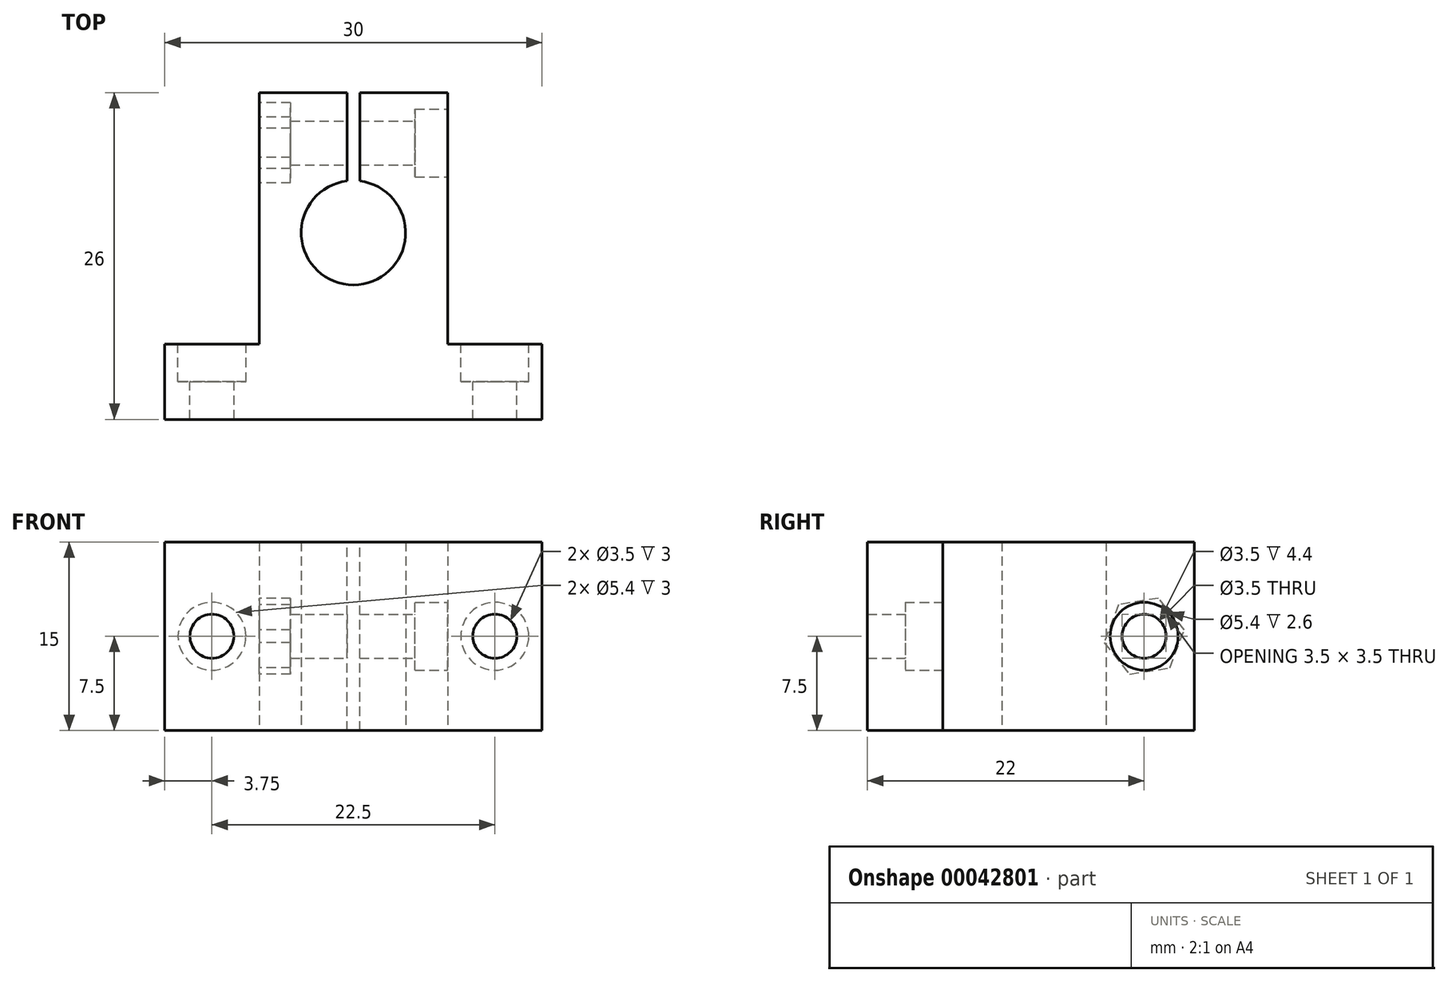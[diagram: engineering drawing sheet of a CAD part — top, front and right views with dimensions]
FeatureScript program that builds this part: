
annotation { "Feature Type Name" : "Feature", "Feature Type Description" : "" }
export const myFeature = defineFeature(function(context is Context, id is Id, definition is map)
    precondition{}
    {
        {
            var Q0;
            Q0=qCreatedBy(makeId("Top.planeOp"),FACE);
            var sketch = newSketch(context, id + "F0", { "sketchPlane" : qUnion([Q0])});
            skLineSegment(sketch, "E0.rect.bottom", {"start": v(-7.5, 10) * mm, "end": v(7.5, 10) * mm});
            skLineSegment(sketch, "E0.rect.left", {"start": v(-7.5, 10) * mm, "end": v(-7.5, -10) * mm});
            skLineSegment(sketch, "E0.rect.right", {"start": v(7.5, 10) * mm, "end": v(7.5, -10) * mm});
            skLineSegment(sketch, "E1.top", {"start": v(-15, -16) * mm, "end": v(15, -16) * mm});
            skLineSegment(sketch, "E1.left", {"start": v(-15, -10) * mm, "end": v(-15, -16) * mm});
            skLineSegment(sketch, "E1.right", {"start": v(15, -10) * mm, "end": v(15, -16) * mm});
            skLineSegment(sketch, "E2", {"start": v(-15, -10) * mm, "end": v(-7.5, -10) * mm});
            skLineSegment(sketch, "E3", {"start": v(7.5, -10) * mm, "end": v(15, -10) * mm});
            skCircle(sketch, "E4", {"center": v(0, -1.15) * mm, "radius": 4.15 * mm});
            skSolve(sketch);
        }
        {
            var Q0;
            {var subQ2=sQuery(id+"F0.wireOp",EDGE,"E0.rect.left");Q0=makeQuery(id+"F0.imprint","IMPRINT",FACE,{"disambiguationData":[TD([[makeQuery(id+"F0.imprint","IMPRINT",EDGE,{"derivedFrom":subQ2}),1.0]])]});}
            extrude(context, id + "F1", {"entities" : qUnion([Q0]), "depth" : 15 * mm});
        }
        {
            var Q0;
            Q0=makeQuery(id+"F1.opExtrude","SWEPT_FACE",FACE,{"disambiguationData":[OSD([sQuery(id+"F0.wireOp",EDGE,"E0.rect.bottom")])]});
            var sketch = newSketch(context, id + "F2", { "sketchPlane" : qUnion([Q0])});
            skLineSegment(sketch, "E5.bottom", {"start": v(0.5, 0) * mm, "end": v(-0.5, 0) * mm});
            skLineSegment(sketch, "E5.top", {"start": v(0.5, 15) * mm, "end": v(-0.5, 15) * mm});
            skLineSegment(sketch, "E5.left", {"start": v(0.5, 0) * mm, "end": v(0.5, 15) * mm});
            skLineSegment(sketch, "E5.right", {"start": v(-0.5, 0) * mm, "end": v(-0.5, 15) * mm});
            skSolve(sketch);
        }
        {
            var Q0;
            Q0=makeQuery(id+"F2.imprint","IMPRINT",FACE,{"disambiguationData":[TD([[makeQuery(id+"F2.imprint","IMPRINT",EDGE,{"derivedFrom":sQuery(id+"F2.wireOp",EDGE,"E5.bottom")}),-1.0]])]});
            extrude(context, id + "F3", {"entities" : qUnion([Q0]), "operationType" : NewBodyOperationType.REMOVE, "oppositeDirection" : true, "depth" : 10 * mm});
        }
        {
            var Q0;
            Q0=makeQuery(id+"F1.opExtrude","SWEPT_FACE",FACE,{"disambiguationData":[OSD([sQuery(id+"F0.wireOp",EDGE,"E0.rect.right")])]});
            var sketch = newSketch(context, id + "F4", { "sketchPlane" : qUnion([Q0])});
            skCircle(sketch, "E6", {"center": v(6, 7.5) * mm, "radius": 1.75 * mm});
            skCircle(sketch, "E7", {"center": v(6, 7.5) * mm, "radius": 2.7 * mm});
            skSolve(sketch);
        }
        {
            var Q0;
            Q0=makeQuery(id+"F1.opExtrude","SWEPT_FACE",FACE,{"disambiguationData":[OSD([sQuery(id+"F0.wireOp",EDGE,"E3")])]});
            var sketch = newSketch(context, id + "F5", { "sketchPlane" : qUnion([Q0])});
            skCircle(sketch, "E8", {"center": v(-11.25, 7.5) * mm, "radius": 1.75 * mm});
            skCircle(sketch, "E9", {"center": v(-11.25, 7.5) * mm, "radius": 2.7 * mm});
            skSolve(sketch);
        }
        {
            var Q0;
            Q0=sQuery(id+"F5.wireOp",VERTEX,"E8.center");
            var Q1;
            Q1=makeQuery(id+"F1.opExtrude","SWEPT_BODY",BODY,{"disambiguationData":[OSD([sQuery(id+"F0.wireOp",EDGE,"E0.rect.bottom"),sQuery(id+"F0.wireOp",EDGE,"E0.rect.left"),sQuery(id+"F0.wireOp",EDGE,"E0.rect.right"),sQuery(id+"F0.wireOp",EDGE,"E1.top"),sQuery(id+"F0.wireOp",EDGE,"E1.left"),sQuery(id+"F0.wireOp",EDGE,"E1.right"),sQuery(id+"F0.wireOp",EDGE,"E2"),sQuery(id+"F0.wireOp",EDGE,"E3"),sQuery(id+"F0.wireOp",EDGE,"b83604dc-ecee-46dd-b54f-97ce1fcc9892")])]});
            hole(context, id + "F6", {"style" : HoleStyle.SIMPLE, "holeDiameter" : 3.5 * mm, "endStyle" : HoleEndStyle.THROUGH, "locations" : qUnion([Q0]), "scope" : qUnion([Q1])});
        }
        {
            var Q0;
            Q0=makeQuery(id+"F1.opExtrude","SWEPT_FACE",FACE,{"disambiguationData":[OSD([sQuery(id+"F0.wireOp",EDGE,"E2")])]});
            var sketch = newSketch(context, id + "F7", { "sketchPlane" : qUnion([Q0])});
            skCircle(sketch, "E10", {"center": v(11.25, 7.5) * mm, "radius": 1.75 * mm});
            skCircle(sketch, "E11", {"center": v(11.25, 7.5) * mm, "radius": 2.7 * mm});
            skSolve(sketch);
        }
        {
            var Q0;
            Q0=makeQuery(id+"F7.imprint","IMPRINT",FACE,{"disambiguationData":[TD([[makeQuery(id+"F7.imprint","IMPRINT",EDGE,{"derivedFrom":sQuery(id+"F7.wireOp",EDGE,"E10")}),1.0]])]});
            extrude(context, id + "F8", {"entities" : qUnion([Q0]), "operationType" : NewBodyOperationType.REMOVE, "oppositeDirection" : true, "depth" : 25 * mm});
        }
        {
            var Q0;
            Q0=makeQuery(id+"F4.imprint","IMPRINT",FACE,{"disambiguationData":[TD([[makeQuery(id+"F4.imprint","IMPRINT",EDGE,{"derivedFrom":sQuery(id+"F4.wireOp",EDGE,"E6")}),1.0]])]});
            extrude(context, id + "F9", {"entities" : qUnion([Q0]), "operationType" : NewBodyOperationType.REMOVE, "endBound" : BoundingType.THROUGH_ALL, "oppositeDirection" : true, "depth" : 25 * mm});
        }
        {
            var Q0;
            Q0=makeQuery(id+"F1.opExtrude","SWEPT_FACE",FACE,{"disambiguationData":[OSD([sQuery(id+"F0.wireOp",EDGE,"E0.rect.left")])]});
            var sketch = newSketch(context, id + "F10", { "sketchPlane" : qUnion([Q0])});
            skCircle(sketch, "E12.cCircle", {"center": v(-6, 7.5) * mm, "radius": 2.8 * mm, "construction": true});
            skLineSegment(sketch, "E12.0", {"start": v(-9.2, 8.01) * mm, "end": v(-7.15, 10.52) * mm});
            skLineSegment(sketch, "E12.1", {"start": v(-7.15, 10.52) * mm, "end": v(-3.96, 10) * mm});
            skLineSegment(sketch, "E12.2", {"start": v(-3.96, 10) * mm, "end": v(-2.8, 6.99) * mm});
            skLineSegment(sketch, "E12.3", {"start": v(-2.8, 6.99) * mm, "end": v(-4.85, 4.48) * mm});
            skLineSegment(sketch, "E12.4", {"start": v(-4.85, 4.48) * mm, "end": v(-8.04, 5) * mm});
            skLineSegment(sketch, "E12.5", {"start": v(-8.04, 5) * mm, "end": v(-9.2, 8.01) * mm});
            skPoint(sketch, "E12.0.midPoint", {"position": v(-8.17, 9.27) * mm});
            skSolve(sketch);
        }
        {
            var Q0;
            Q0=makeQuery(id+"F10.imprint","IMPRINT",FACE,{"disambiguationData":[TD([[makeQuery(id+"F10.imprint","IMPRINT",EDGE,{"derivedFrom":sQuery(id+"F10.wireOp",EDGE,"E12.0")}),-1.0]])]});
            extrude(context, id + "F11", {"entities" : qUnion([Q0]), "operationType" : NewBodyOperationType.REMOVE, "oppositeDirection" : true, "depth" : 2.5 * mm});
        }
        {
            var Q0;
            Q0=makeQuery(id+"F4.imprint","IMPRINT",FACE,{"disambiguationData":[TD([[makeQuery(id+"F4.imprint","IMPRINT",EDGE,{"derivedFrom":sQuery(id+"F4.wireOp",EDGE,"E6")}),-1.0]])]});
            extrude(context, id + "F12", {"entities" : qUnion([Q0]), "operationType" : NewBodyOperationType.REMOVE, "oppositeDirection" : true, "depth" : 2.6 * mm});
        }
        {
            var Q0;
            Q0 = qSketchRegion(id + "F7", true);
            extrude(context, id + "F13", {"entities" : qUnion([Q0]), "operationType" : NewBodyOperationType.REMOVE, "oppositeDirection" : true, "depth" : 3 * mm});
        }
        {
            var Q0;
            Q0 = qSketchRegion(id + "F5", true);
            extrude(context, id + "F14", {"entities" : qUnion([Q0]), "operationType" : NewBodyOperationType.REMOVE, "oppositeDirection" : true, "depth" : 3 * mm});
        }
    });
